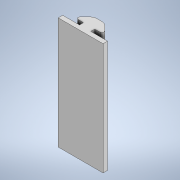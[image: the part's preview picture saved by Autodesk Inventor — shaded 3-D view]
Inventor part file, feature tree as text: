
AUTODESK INVENTOR PART (.ipt)
format: ipt  version: 2020 (Build 240168000, 168)  size: 135,680 bytes
history: native  units: mm
features: other x1, extrude x1, sketch x1
ambient origin geometry x8: Origin, YZ Plane, XZ Plane, XY Plane, X Axis, Y Axis, Z Axis, Center Point
bodies: Body1 (feature_tree)
feature tree (3):
  other  "Bryła1"
  extrude  "Wyciągnięcie proste1"  Depth=2.0mm
  sketch  "Szkic1"
